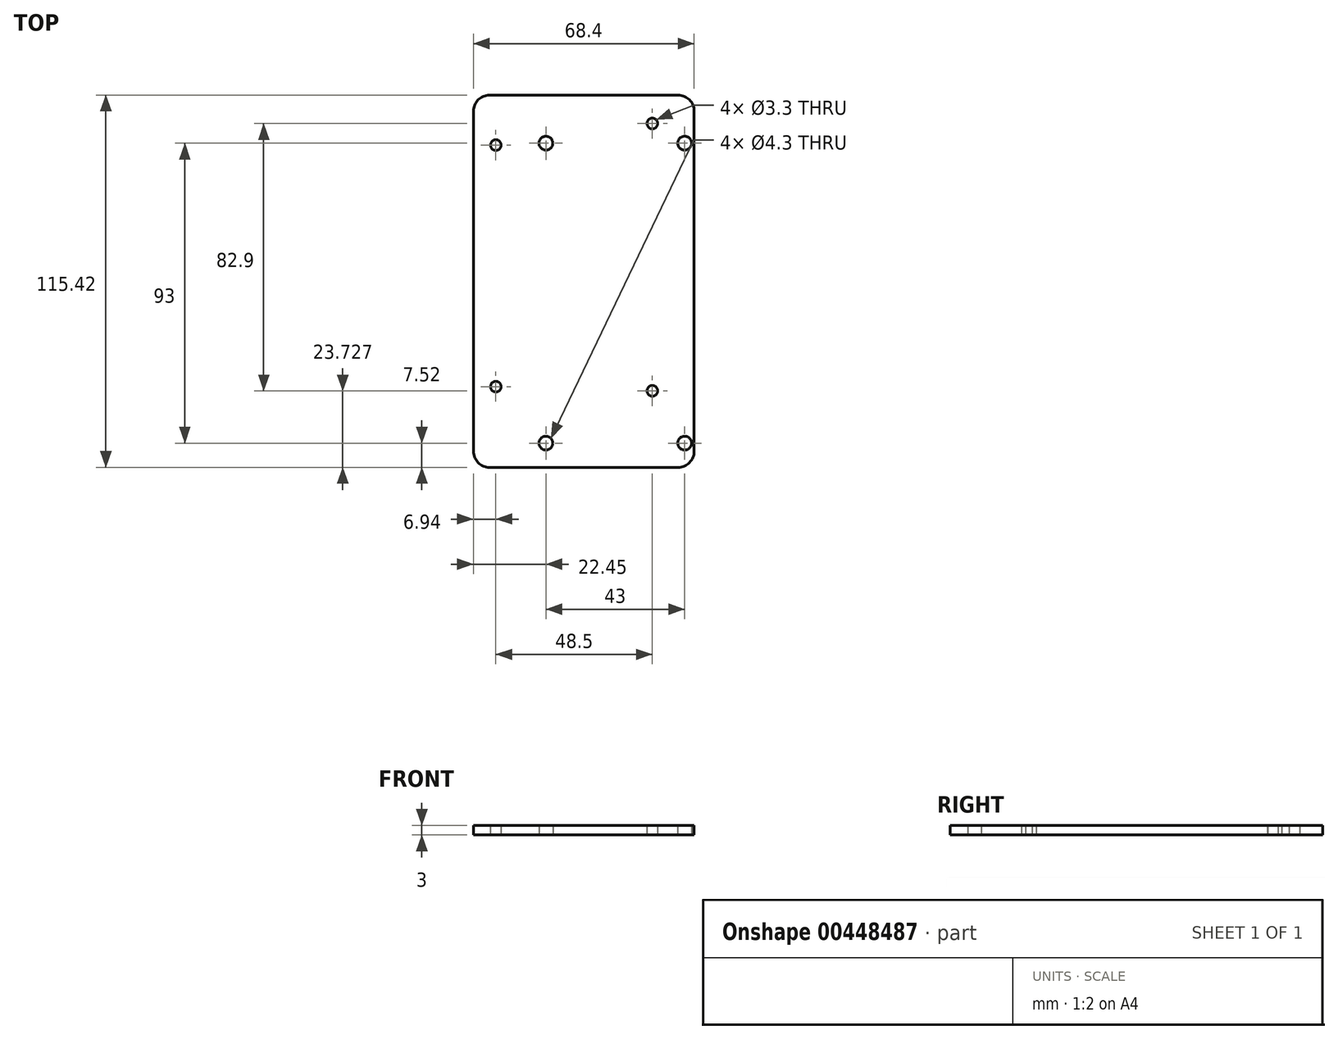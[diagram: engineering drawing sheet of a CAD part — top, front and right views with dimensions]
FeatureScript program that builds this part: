
annotation { "Feature Type Name" : "Feature", "Feature Type Description" : "" }
export const myFeature = defineFeature(function(context is Context, id is Id, definition is map)
    precondition{}
    {
        {
            var Q0;
            Q0=qCreatedBy(makeId("Top.planeOp"),FACE);
            var sketch = newSketch(context, id + "F0", { "sketchPlane" : qUnion([Q0])});
            skLineSegment(sketch, "E0.bottom", {"start": v(-21.5, 46.5) * mm, "end": v(21.5, 46.5) * mm, "construction": true});
            skLineSegment(sketch, "E0.top", {"start": v(-21.5, -46.5) * mm, "end": v(21.5, -46.5) * mm, "construction": true});
            skLineSegment(sketch, "E0.left", {"start": v(-21.5, 46.5) * mm, "end": v(-21.5, -46.5) * mm, "construction": true});
            skLineSegment(sketch, "E0.right", {"start": v(21.5, 46.5) * mm, "end": v(21.5, -46.5) * mm, "construction": true});
            skPoint(sketch, "E0.middle", {"position": v(0, 0) * mm});
            skLineSegment(sketch, "E1.bottom", {"start": v(24.45, -54.02) * mm, "end": v(-43.95, -54.02) * mm});
            skLineSegment(sketch, "E1.left", {"start": v(24.45, -54.02) * mm, "end": v(24.45, 61.4) * mm});
            skLineSegment(sketch, "E2", {"start": v(-43.95, 45.2) * mm, "end": v(-43.95, -54.02) * mm});
            skLineSegment(sketch, "E3", {"start": v(-37.01, 45.9) * mm, "end": v(-37.01, -29) * mm, "construction": true});
            skLineSegment(sketch, "E4", {"start": v(11.49, 52.6) * mm, "end": v(11.49, -30.3) * mm, "construction": true});
            skLineSegment(sketch, "E5", {"start": v(15.34, -29) * mm, "end": v(117.39, -29) * mm, "construction": true});
            skLineSegment(sketch, "E6", {"start": v(-43.95, 45.2) * mm, "end": v(-43.95, 61.4) * mm});
            skLineSegment(sketch, "E7", {"start": v(-43.95, 61.4) * mm, "end": v(24.45, 61.4) * mm});
            skSolve(sketch);
        }
        {
            var Q0;
            Q0=qSketchRegion(id+"F0",true);
            extrude(context, id + "F1", {"entities" : qUnion([Q0]), "depth" : 3 * mm, "offsetDistance" : 25 * mm});
        }
        {
            var Q0;
            Q0=sQuery(id+"F0.wireOp",VERTEX,"J893LHRk-zqBD-1rvg-63pD-eBwt5VtB3pDJ.top.end");
            var Q1;
            Q1=sQuery(id+"F0.wireOp",VERTEX,"J893LHRk-zqBD-1rvg-63pD-eBwt5VtB3pDJ.bottom.end");
            var Q2;
            Q2=sQuery(id+"F0.wireOp",VERTEX,"J893LHRk-zqBD-1rvg-63pD-eBwt5VtB3pDJ.bottom.start");
            var Q3;
            Q3=sQuery(id+"F0.wireOp",VERTEX,"J893LHRk-zqBD-1rvg-63pD-eBwt5VtB3pDJ.left.end");
            var Q4;
            Q4=sQuery(id+"F0.wireOp",VERTEX,"4N1vUwWh-xHJR-HAm5-r41G-x5FdNC7RSBuu.right.end");
            var Q5;
            Q5=sQuery(id+"F0.wireOp",VERTEX,"4N1vUwWh-xHJR-HAm5-r41G-x5FdNC7RSBuu.top.start");
            var Q6;
            Q6=sQuery(id+"F0.wireOp",VERTEX,"4N1vUwWh-xHJR-HAm5-r41G-x5FdNC7RSBuu.right.start");
            var Q7;
            Q7=sQuery(id+"F0.wireOp",VERTEX,"4N1vUwWh-xHJR-HAm5-r41G-x5FdNC7RSBuu.bottom.start");
            var Q8;
            Q8=sQuery(id+"F0.wireOp",VERTEX,"E3.start");
            var Q9;
            Q9=sQuery(id+"F0.wireOp",VERTEX,"E4.start");
            var Q10;
            Q10=sQuery(id+"F0.wireOp",VERTEX,"E4.end");
            var Q11;
            Q11=sQuery(id+"F0.wireOp",VERTEX,"E3.end");
            var Q12;
            Q12=makeQuery(id+"F1.opExtrude","SWEPT_BODY",BODY,{"disambiguationData":[OSD([sQuery(id+"F0.wireOp",EDGE,"E1.bottom"),sQuery(id+"F0.wireOp",EDGE,"E1.top"),sQuery(id+"F0.wireOp",EDGE,"E1.left"),sQuery(id+"F0.wireOp",EDGE,"E1.right"),sQuery(id+"F0.wireOp",EDGE,"E2"),sQuery(id+"F0.wireOp",EDGE,"XyIVaQW3-El7N-e6bz-1eAk-mJc9jGYG2OAW"),sQuery(id+"F0.wireOp",EDGE,"2inYUX5w-coaZ-2hAe-3aFK-Vs1NiTnumc5f"),sQuery(id+"F0.wireOp",EDGE,"RIFZKn75-bQRI-PPT5-OLLJ-XKhDclTj2aRo")])]});
            hole(context, id + "F2", {"style" : HoleStyle.SIMPLE, "endStyle" : HoleEndStyle.THROUGH, "oppositeDirection" : true, "standardTappedOrClearance" : lookupTablePath({ "standard" : "ISO", "fit" : "Normal", "size" : "M3", "type" : "Clearance" }), "standardBlindInLast" : lookupTablePath({ "fit" : "Standard", "standard" : "ISO", "size" : "M3", "type" : "Clearance" }), "holeDiameter" : 3.3 * mm, "majorDiameter" : 5 * mm, "isTappedThrough" : true, "tappedDepth" : 12 * mm, "tapClearance" : 3, "startFromSketch" : true, "locations" : qUnion([Q0, Q1, Q2, Q3, Q4, Q5, Q6, Q7, Q8, Q9, Q10, Q11]), "scope" : qUnion([Q12])});
        }
        {
            var Q0;
            Q0=sQuery(id+"F0.wireOp",VERTEX,"E0.left.start");
            var Q1;
            Q1=sQuery(id+"F0.wireOp",VERTEX,"E0.right.start");
            var Q2;
            Q2=sQuery(id+"F0.wireOp",VERTEX,"E0.right.end");
            var Q3;
            Q3=sQuery(id+"F0.wireOp",VERTEX,"E0.left.end");
            var Q4;
            Q4=makeQuery(id+"F1.opExtrude","SWEPT_BODY",BODY,{"disambiguationData":[OSD([sQuery(id+"F0.wireOp",EDGE,"E1.bottom"),sQuery(id+"F0.wireOp",EDGE,"E1.top"),sQuery(id+"F0.wireOp",EDGE,"E1.left"),sQuery(id+"F0.wireOp",EDGE,"E1.right"),sQuery(id+"F0.wireOp",EDGE,"E2"),sQuery(id+"F0.wireOp",EDGE,"XyIVaQW3-El7N-e6bz-1eAk-mJc9jGYG2OAW"),sQuery(id+"F0.wireOp",EDGE,"2inYUX5w-coaZ-2hAe-3aFK-Vs1NiTnumc5f"),sQuery(id+"F0.wireOp",EDGE,"RIFZKn75-bQRI-PPT5-OLLJ-XKhDclTj2aRo")])]});
            hole(context, id + "F3", {"style" : HoleStyle.SIMPLE, "endStyle" : HoleEndStyle.THROUGH, "oppositeDirection" : true, "holeDiameter" : 4.3 * mm, "majorDiameter" : 5 * mm, "isTappedThrough" : true, "tappedDepth" : 12 * mm, "tapClearance" : 3, "startFromSketch" : true, "locations" : qUnion([Q0, Q1, Q2, Q3]), "scope" : qUnion([Q4])});
        }
        {
            var Q0;
            Q0=makeQuery(id+"F1.opExtrude","SWEPT_EDGE",EDGE,{"disambiguationData":[OSD([sQuery(id+"F0.wireOp",EDGE,"E1.top"),sQuery(id+"F0.wireOp",EDGE,"E1.right")])]});
            var Q1;
            Q1=makeQuery(id+"F1.opExtrude","SWEPT_EDGE",EDGE,{"disambiguationData":[OSD([sQuery(id+"F0.wireOp",EDGE,"XyIVaQW3-El7N-e6bz-1eAk-mJc9jGYG2OAW"),sQuery(id+"F0.wireOp",EDGE,"2inYUX5w-coaZ-2hAe-3aFK-Vs1NiTnumc5f")])]});
            var Q2;
            Q2=makeQuery(id+"F1.opExtrude","SWEPT_EDGE",EDGE,{"disambiguationData":[OSD([sQuery(id+"F0.wireOp",EDGE,"E2"),sQuery(id+"F0.wireOp",EDGE,"XyIVaQW3-El7N-e6bz-1eAk-mJc9jGYG2OAW")])]});
            var Q3;
            Q3=makeQuery(id+"F1.opExtrude","SWEPT_EDGE",EDGE,{"disambiguationData":[OSD([sQuery(id+"F0.wireOp",EDGE,"E2"),sQuery(id+"F0.wireOp",EDGE,"RIFZKn75-bQRI-PPT5-OLLJ-XKhDclTj2aRo")])]});
            var Q4;
            Q4=makeQuery(id+"F1.opExtrude","SWEPT_EDGE",EDGE,{"disambiguationData":[OSD([sQuery(id+"F0.wireOp",EDGE,"E1.bottom"),sQuery(id+"F0.wireOp",EDGE,"2inYUX5w-coaZ-2hAe-3aFK-Vs1NiTnumc5f")])]});
            var Q5;
            Q5=makeQuery(id+"F1.opExtrude","SWEPT_EDGE",EDGE,{"disambiguationData":[OSD([sQuery(id+"F0.wireOp",EDGE,"E1.right"),sQuery(id+"F0.wireOp",EDGE,"RIFZKn75-bQRI-PPT5-OLLJ-XKhDclTj2aRo")])]});
            var Q6;
            Q6=makeQuery(id+"F1.opExtrude","SWEPT_EDGE",EDGE,{"disambiguationData":[OSD([sQuery(id+"F0.wireOp",EDGE,"E1.top"),sQuery(id+"F0.wireOp",EDGE,"E1.left")])]});
            var Q7;
            Q7=makeQuery(id+"F1.opExtrude","SWEPT_EDGE",EDGE,{"disambiguationData":[OSD([sQuery(id+"F0.wireOp",EDGE,"E1.bottom"),sQuery(id+"F0.wireOp",EDGE,"E1.left")])]});
            var Q8;
            Q8=makeQuery(id+"F1.opExtrude","SWEPT_EDGE",EDGE,{"disambiguationData":[OSD([sQuery(id+"F0.wireOp",EDGE,"Mbf7E7DW-qALH-cvkv-Damv-hvnqM2JEZsVI"),sQuery(id+"F0.wireOp",EDGE,"yL2UZmJc-QStA-b8Vo-1v86-bxjpKFNwprbL")])]});
            var Q9;
            Q9=makeQuery(id+"F1.opExtrude","SWEPT_EDGE",EDGE,{"disambiguationData":[OSD([sQuery(id+"F0.wireOp",EDGE,"qiIUHCKB-fCWY-SWhl-cjjz-M1Dty9vsqyQJ"),sQuery(id+"F0.wireOp",EDGE,"Q55u8Cbf-FWXE-ZP9w-DCtp-IPOpDFhRQxLW")])]});
            var Q10;
            Q10=makeQuery(id+"F1.opExtrude","SWEPT_EDGE",EDGE,{"disambiguationData":[OSD([sQuery(id+"F0.wireOp",EDGE,"a1f7CNFQ-nP29-92E3-ja6P-g6eo9MA6HpaG"),sQuery(id+"F0.wireOp",EDGE,"OeeX4dYa-ce1g-dk9C-RiQx-GZsGsBV5ChxM")])]});
            var Q11;
            Q11=makeQuery(id+"F1.opExtrude","SWEPT_EDGE",EDGE,{"disambiguationData":[OSD([sQuery(id+"F0.wireOp",EDGE,"OeeX4dYa-ce1g-dk9C-RiQx-GZsGsBV5ChxM"),sQuery(id+"F0.wireOp",EDGE,"j85sN3cy-DIR5-E17b-kCIM-lPXGn6SRW4FC")])]});
            var Q12;
            Q12=makeQuery(id+"F1.opExtrude","SWEPT_EDGE",EDGE,{"disambiguationData":[OSD([sQuery(id+"F0.wireOp",EDGE,"H5cnSjnK-4Nrg-yr1O-NTxU-GIKtI7yp09dG"),sQuery(id+"F0.wireOp",EDGE,"aUoxsp5O-AR9o-Et6y-4KpD-5wgRAlL37lOh")])]});
            var Q13;
            Q13=makeQuery(id+"F1.opExtrude","SWEPT_EDGE",EDGE,{"disambiguationData":[OSD([sQuery(id+"F0.wireOp",EDGE,"9UlV4Nop-iNJr-02NP-fapv-DWM8Iypxcy4n"),sQuery(id+"F0.wireOp",EDGE,"RAkMmiOb-nROR-mXBJ-D0fB-59uvw5uzIgUD")])]});
            var Q14;
            Q14=makeQuery(id+"F1.opExtrude","SWEPT_EDGE",EDGE,{"disambiguationData":[OSD([sQuery(id+"F0.wireOp",EDGE,"RpWV4TA2-qZx3-hfFS-Fjk5-bPTjN17klhtH"),sQuery(id+"F0.wireOp",EDGE,"2l11ivdO-LSoy-1MMf-z1oK-tAifx8Baqm9W")])]});
            var Q15;
            Q15=makeQuery(id+"F1.opExtrude","SWEPT_EDGE",EDGE,{"disambiguationData":[OSD([sQuery(id+"F0.wireOp",EDGE,"E6"),sQuery(id+"F0.wireOp",EDGE,"E7")])]});
            fillet(context, id + "F4", {"entities" : qUnion([Q0, Q1, Q2, Q3, Q4, Q5, Q6, Q7, Q8, Q9, Q10, Q11, Q12, Q13, Q14, Q15]), "radius" : 5 * mm, "tangentPropagation" : true, "allowEdgeOverflow" : false});
        }
    });
